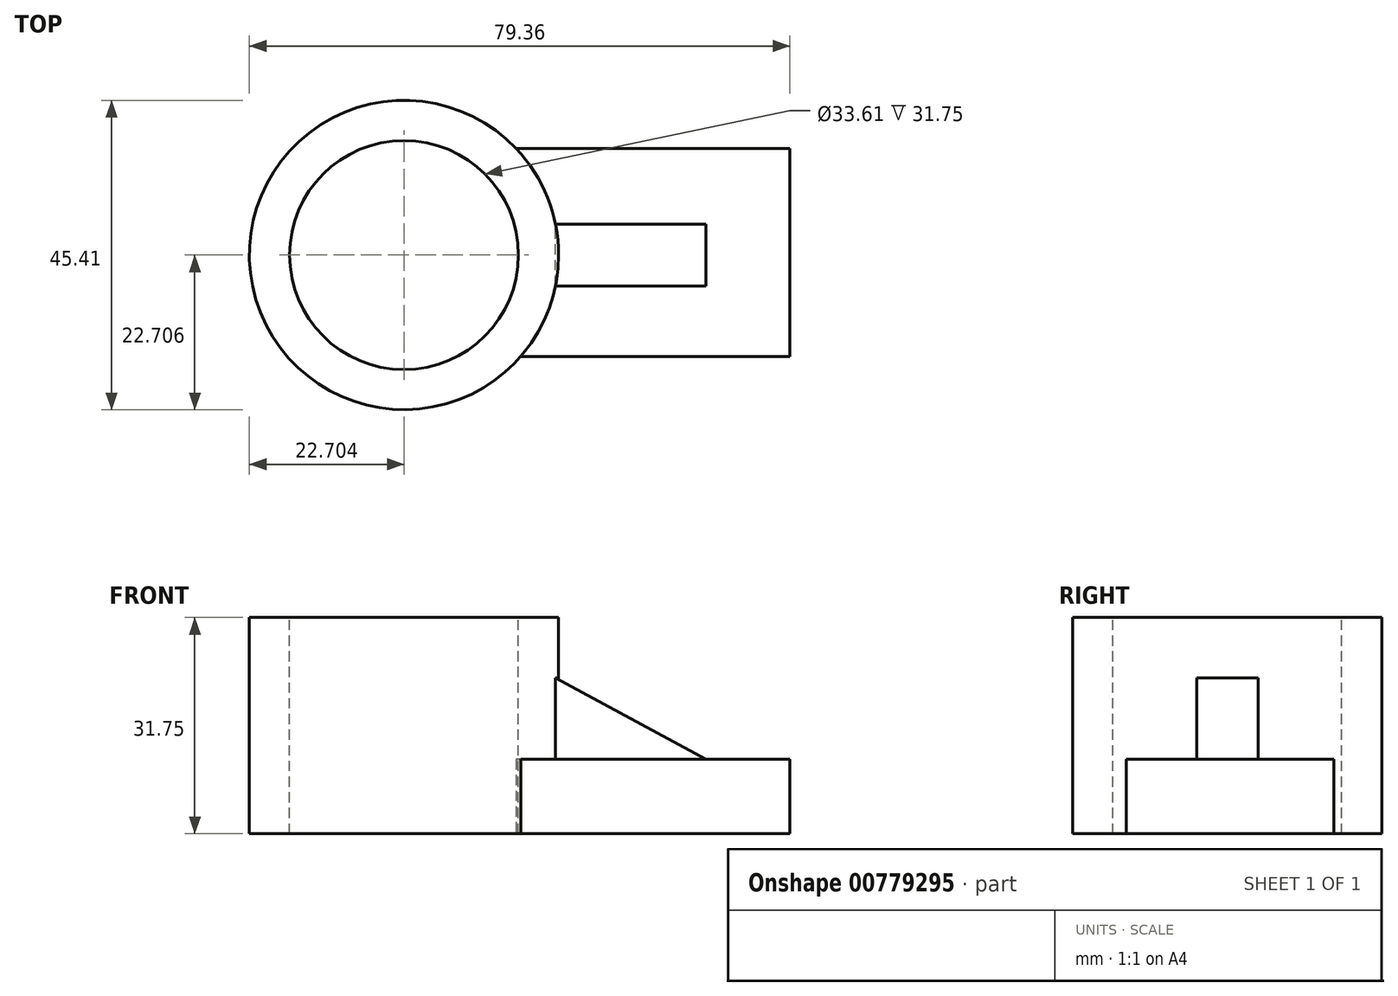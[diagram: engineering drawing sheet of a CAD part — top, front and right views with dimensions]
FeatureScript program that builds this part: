
annotation { "Feature Type Name" : "Feature", "Feature Type Description" : "" }
export const myFeature = defineFeature(function(context is Context, id is Id, definition is map)
    precondition{}
    {
        {
            var Q0;
            Q0=qCreatedBy(makeId("Top.planeOp"),FACE);
            var sketch = newSketch(context, id + "F0", { "sketchPlane" : qUnion([Q0])});
            skLineSegment(sketch, "E0.bottom", {"start": v(-44.86, -38.27) * mm, "end": v(12.3, -38.27) * mm});
            skLineSegment(sketch, "E0.top", {"start": v(-44.86, -7.76) * mm, "end": v(12.3, -7.76) * mm});
            skLineSegment(sketch, "E0.left", {"start": v(-44.86, -38.27) * mm, "end": v(-44.86, -7.76) * mm});
            skLineSegment(sketch, "E0.right", {"start": v(12.3, -38.27) * mm, "end": v(12.3, -7.76) * mm});
            skSolve(sketch);
        }
        {
            var Q0;
            Q0=makeQuery(id+"F0.imprint","IMPRINT",FACE,{"disambiguationData":[TD([[makeQuery(id+"F0.imprint","IMPRINT",EDGE,{"derivedFrom":sQuery(id+"F0.wireOp",EDGE,"E0.bottom")}),1.0]])]});
            var sketch = newSketch(context, id + "F1", { "sketchPlane" : qUnion([Q0])});
            skCircle(sketch, "E1", {"center": v(-44.35, -23.4) * mm, "radius": 22.7 * mm});
            skSolve(sketch);
        }
        {
            var Q0;
            Q0 = qSketchRegion(id + "F1", true);
            extrude(context, id + "F2", {"entities" : qUnion([Q0]), "depth" : 31.75 * mm, "offsetDistance" : 25.4 * mm});
        }
        {
            var Q0;
            Q0=makeQuery(id+"F0.imprint","IMPRINT",FACE,{"disambiguationData":[TD([[makeQuery(id+"F0.imprint","IMPRINT",EDGE,{"derivedFrom":sQuery(id+"F0.wireOp",EDGE,"E0.bottom")}),1.0]])]});
            extrude(context, id + "F3", {"entities" : qUnion([Q0]), "operationType" : NewBodyOperationType.ADD, "depth" : 10.92 * mm, "offsetDistance" : 25.4 * mm});
        }
        {
            var Q0;
            Q0=makeQuery(id+"F2.opExtrude","CAP_FACE",FACE,{"disambiguationData":[OSD([sQuery(id+"F1.wireOp",EDGE,"E1")])],"isStart":false});
            var sketch = newSketch(context, id + "F4", { "sketchPlane" : qUnion([Q0])});
            skCircle(sketch, "E2", {"center": v(-44.35, -23.4) * mm, "radius": 16.8 * mm});
            skSolve(sketch);
        }
        {
            var Q0;
            Q0 = qSketchRegion(id + "F4", true);
            extrude(context, id + "F5", {"entities" : qUnion([Q0]), "operationType" : NewBodyOperationType.REMOVE, "oppositeDirection" : true, "depth" : 45.47 * mm, "offsetDistance" : 25.4 * mm});
        }
        {
            var Q0;
            Q0=makeQuery(id+"F3.opExtrude","CAP_FACE",FACE,{"disambiguationData":[OSD([sQuery(id+"F0.wireOp",EDGE,"E0.bottom"),sQuery(id+"F0.wireOp",EDGE,"E0.top"),sQuery(id+"F0.wireOp",EDGE,"E0.left"),sQuery(id+"F0.wireOp",EDGE,"E0.right")])],"isStart":false});
            var sketch = newSketch(context, id + "F6", { "sketchPlane" : qUnion([Q0])});
            skLineSegment(sketch, "E3.bottom", {"start": v(0, -27.92) * mm, "end": v(-22.1, -27.92) * mm});
            skLineSegment(sketch, "E3.top", {"start": v(0, -18.88) * mm, "end": v(-22.1, -18.88) * mm});
            skLineSegment(sketch, "E3.left", {"start": v(0, -27.92) * mm, "end": v(0, -18.88) * mm});
            skLineSegment(sketch, "E3.right", {"start": v(-22.1, -27.92) * mm, "end": v(-22.1, -18.88) * mm});
            skSolve(sketch);
        }
        {
            var Q0;
            Q0 = qSketchRegion(id + "F6", true);
            extrude(context, id + "F7", {"entities" : qUnion([Q0]), "operationType" : NewBodyOperationType.ADD, "depth" : 11.94 * mm, "offsetDistance" : 25.4 * mm});
        }
        {
            var Q0;
            Q0=makeQuery(id+"F7.opExtrude","SWEPT_FACE",FACE,{"disambiguationData":[OSD([sQuery(id+"F6.wireOp",EDGE,"E3.top")])]});
            var sketch = newSketch(context, id + "F8", { "sketchPlane" : qUnion([Q0])});
            skLineSegment(sketch, "E4", {"start": v(22.1, 22.86) * mm, "end": v(0, 10.92) * mm});
            skLineSegment(sketch, "E5", {"start": v(0, 10.92) * mm, "end": v(0, 22.86) * mm});
            skLineSegment(sketch, "E6", {"start": v(0, 22.86) * mm, "end": v(22.1, 22.86) * mm});
            skSolve(sketch);
        }
        {
            var Q0;
            Q0 = qSketchRegion(id + "F8", true);
            extrude(context, id + "F9", {"entities" : qUnion([Q0]), "operationType" : NewBodyOperationType.REMOVE, "oppositeDirection" : true, "depth" : 25.4 * mm, "offsetDistance" : 25.4 * mm});
        }
    });
